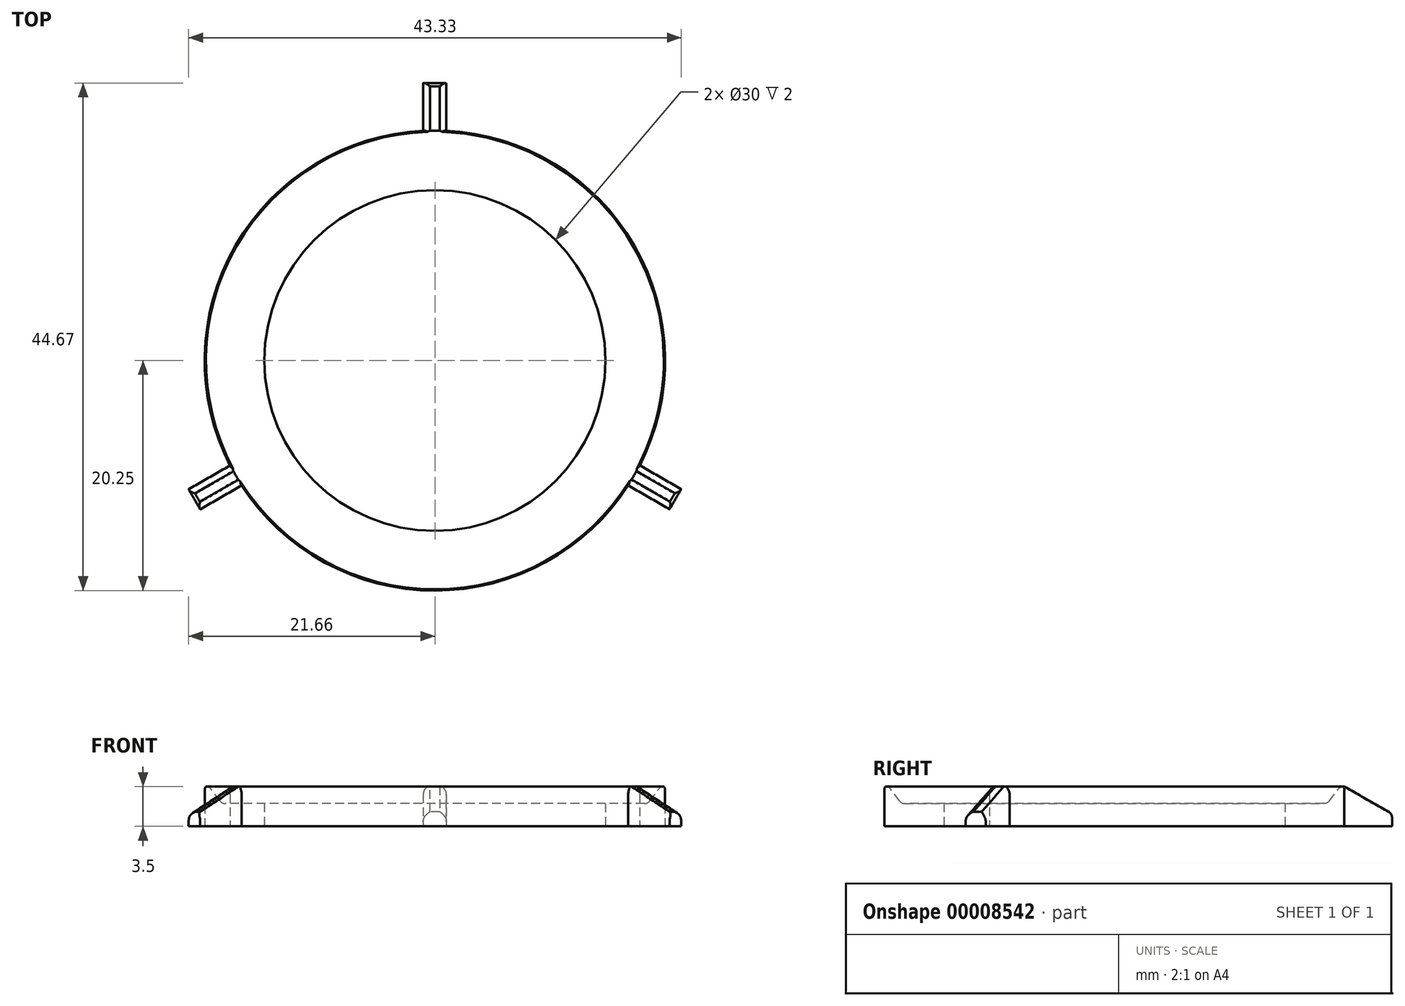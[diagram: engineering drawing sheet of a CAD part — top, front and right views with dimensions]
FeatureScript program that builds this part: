
annotation { "Feature Type Name" : "Feature", "Feature Type Description" : "" }
export const myFeature = defineFeature(function(context is Context, id is Id, definition is map)
    precondition{}
    {
        {
            var Q0;
            Q0=qCreatedBy(makeId("Top.planeOp"),FACE);
            var sketch = newSketch(context, id + "F0", { "sketchPlane" : qUnion([Q0])});
            skCircle(sketch, "E0", {"center": v(0, 0) * mm, "radius": 20.25 * mm});
            skCircle(sketch, "E1", {"center": v(0, 0) * mm, "radius": 15 * mm});
            skLineSegment(sketch, "E2", {"start": v(-1.03, 24.42) * mm, "end": v(-1.03, 20.22) * mm});
            skLineSegment(sketch, "E3", {"start": v(-1.03, 24.42) * mm, "end": v(0, 24.42) * mm});
            skLineSegment(sketch, "E4.trimOffspring", {"start": v(0, 24.4) * mm, "end": v(0, 24.42) * mm, "construction": true});
            skLineSegment(sketch, "E5", {"start": v(0, 24.42) * mm, "end": v(1.01, 24.42) * mm});
            skLineSegment(sketch, "E6", {"start": v(1.01, 24.42) * mm, "end": v(1.01, 20.22) * mm});
            skLineSegment(sketch, "E7.1.0", {"start": v(-20.64, -13.1) * mm, "end": v(-17, -11) * mm});
            skLineSegment(sketch, "E7.1.1", {"start": v(-20.64, -13.1) * mm, "end": v(-21.15, -12.22) * mm});
            skLineSegment(sketch, "E7.1.2", {"start": v(-21.15, -12.22) * mm, "end": v(-21.66, -11.34) * mm});
            skLineSegment(sketch, "E7.1.3", {"start": v(-21.66, -11.34) * mm, "end": v(-18.02, -9.24) * mm});
            skLineSegment(sketch, "E7.2.0", {"start": v(21.67, -11.32) * mm, "end": v(18.03, -9.22) * mm});
            skLineSegment(sketch, "E7.2.1", {"start": v(21.67, -11.32) * mm, "end": v(21.16, -12.2) * mm});
            skLineSegment(sketch, "E7.2.2", {"start": v(21.16, -12.2) * mm, "end": v(20.65, -13.09) * mm});
            skLineSegment(sketch, "E7.2.3", {"start": v(20.65, -13.09) * mm, "end": v(17, -10.99) * mm});
            skCircle(sketch, "E8", {"center": v(0, 0) * mm, "radius": 24.42 * mm, "construction": true});
            skLineSegment(sketch, "E9", {"start": v(0, 0) * mm, "end": v(0, 30.95) * mm, "construction": true});
            skSolve(sketch);
        }
        {
            var Q0;
            Q0 = qSketchRegion(id + "F0", true);
            extrude(context, id + "F1", {"entities" : qUnion([Q0]), "depth" : 6 * mm});
        }
        {
            var Q0;
            Q0=qCreatedBy(makeId("Right.planeOp"),FACE);
            var sketch = newSketch(context, id + "F2", { "sketchPlane" : qUnion([Q0])});
            skLineSegment(sketch, "E10.0.0", {"start": v(20.22, 0) * mm, "end": v(24.6, 0) * mm});
            skLineSegment(sketch, "E10.0.1", {"start": v(24.6, 0) * mm, "end": v(24.68, 6) * mm});
            skLineSegment(sketch, "E10.0.2", {"start": v(24.68, 6) * mm, "end": v(20.22, 6) * mm});
            skLineSegment(sketch, "E10.0.3", {"start": v(20.22, 6) * mm, "end": v(20.22, 0) * mm});
            skLineSegment(sketch, "E11", {"start": v(-15, 0) * mm, "end": v(-15, 6) * mm});
            skLineSegment(sketch, "E12", {"start": v(15, 6) * mm, "end": v(15, 0) * mm});
            skLineSegment(sketch, "E13.0.0", {"start": v(-9.22, 0) * mm, "end": v(20.22, 0) * mm});
            skLineSegment(sketch, "E13.0.1", {"start": v(20.22, 0) * mm, "end": v(20.22, 6) * mm});
            skLineSegment(sketch, "E13.0.2", {"start": v(20.22, 6) * mm, "end": v(-9.22, 6) * mm});
            skLineSegment(sketch, "E13.0.3", {"start": v(-9.22, 6) * mm, "end": v(-9.22, 0) * mm});
            skLineSegment(sketch, "E14", {"start": v(15, 2) * mm, "end": v(20.22, 2) * mm});
            skLineSegment(sketch, "E15", {"start": v(18.72, 2) * mm, "end": v(20.22, 4) * mm});
            skLineSegment(sketch, "E16", {"start": v(0, 0) * mm, "end": v(0, 9.56) * mm, "construction": true});
            skLineSegment(sketch, "E17", {"start": v(24.61, 1) * mm, "end": v(20.22, 3.5) * mm});
            skSolve(sketch);
        }
        {
            var Q0;
            {var subQ0=sQuery(id+"F2.wireOp",EDGE,"E10.0.2");Q0=makeQuery(id+"F2.imprint","IMPRINT",FACE,{"disambiguationData":[TD([[makeQuery(id+"F2.imprint","IMPRINT",EDGE,{"derivedFrom":subQ0}),1.0]])]});}
            var Q1;
            {var subQ5=sQuery(id+"F2.wireOp",EDGE,"E15");Q1=makeQuery(id+"F2.imprint","IMPRINT",FACE,{"disambiguationData":[TD([[makeQuery(id+"F2.imprint","IMPRINT",EDGE,{"derivedFrom":subQ5}),1.0]])]});}
            var Q2;
            Q2=sQuery(id+"F2.wireOp",EDGE,"E16");
            revolve(context, id + "F3", {"operationType" : NewBodyOperationType.REMOVE, "entities" : qUnion([Q0, Q1]), "axis" : qUnion([Q2]), "revolveType" : RevolveType.FULL, "oppositeDirection" : true});
        }
        {
            var Q0;
            Q0=makeQuery(id+"F3.boolean.opBoolean","COPY",EDGE,{"derivedFrom":makeQuery(id+"F3.opRevolve","SWEPT_EDGE",EDGE,{"disambiguationData":[OSD([sQuery(id+"F2.wireOp",EDGE,"E14"),sQuery(id+"F2.wireOp",EDGE,"E15")])]})});
            var Q1;
            Q1=makeQuery(id+"F3.boolean.opBoolean","COPY",EDGE,{"derivedFrom":makeQuery(id+"F3.opRevolve","SWEPT_EDGE",EDGE,{"disambiguationData":[OSD([sQuery(id+"F2.wireOp",EDGE,"E12"),sQuery(id+"F2.wireOp",EDGE,"E14")])]})});
            var Q2;
            Q2=makeQuery(id+"F3.boolean.opBoolean","COPY",EDGE,{"derivedFrom":makeQuery(id+"F3.opRevolve","SWEPT_EDGE",EDGE,{"disambiguationData":[OSD([sQuery(id+"F2.wireOp",EDGE,"E13.0.1"),sQuery(id+"F2.wireOp",EDGE,"E15")])]})});
            var Q3;
            Q3=makeQuery(id+"F3.boolean.opBoolean","INTERSECT",EDGE,{"derivedFrom":[makeQuery(id+"F1.opExtrude","SWEPT_FACE",FACE,{"disambiguationData":[OSD([sQuery(id+"F0.wireOp",EDGE,"E2")])]}),makeQuery(id+"F3.opRevolve","SWEPT_FACE",FACE,{"disambiguationData":[OSD([sQuery(id+"F2.wireOp",EDGE,"E17")])]})]});
            var Q4;
            Q4=makeQuery(id+"F3.boolean.opBoolean","INTERSECT",EDGE,{"derivedFrom":[makeQuery(id+"F1.opExtrude","SWEPT_FACE",FACE,{"disambiguationData":[OSD([sQuery(id+"F0.wireOp",EDGE,"E6")])]}),makeQuery(id+"F3.opRevolve","SWEPT_FACE",FACE,{"disambiguationData":[OSD([sQuery(id+"F2.wireOp",EDGE,"E17")])]})]});
            var Q5;
            Q5=makeQuery(id+"F3.boolean.opBoolean","INTERSECT",EDGE,{"derivedFrom":[makeQuery(id+"F1.opExtrude","SWEPT_FACE",FACE,{"disambiguationData":[OSD([sQuery(id+"F0.wireOp",EDGE,"E3"),sQuery(id+"F0.wireOp",EDGE,"E5")])]}),makeQuery(id+"F3.opRevolve","SWEPT_FACE",FACE,{"disambiguationData":[OSD([sQuery(id+"F2.wireOp",EDGE,"E17")])]})]});
            var Q6;
            Q6=makeQuery(id+"F3.boolean.opBoolean","INTERSECT",EDGE,{"derivedFrom":[makeQuery(id+"F1.opExtrude","SWEPT_FACE",FACE,{"disambiguationData":[OSD([sQuery(id+"F0.wireOp",EDGE,"E7.2.0")])]}),makeQuery(id+"F3.opRevolve","SWEPT_FACE",FACE,{"disambiguationData":[OSD([sQuery(id+"F2.wireOp",EDGE,"E17")])]})]});
            var Q7;
            Q7=makeQuery(id+"F3.boolean.opBoolean","INTERSECT",EDGE,{"derivedFrom":[makeQuery(id+"F1.opExtrude","SWEPT_FACE",FACE,{"disambiguationData":[OSD([sQuery(id+"F0.wireOp",EDGE,"E7.2.1"),sQuery(id+"F0.wireOp",EDGE,"E7.2.2")])]}),makeQuery(id+"F3.opRevolve","SWEPT_FACE",FACE,{"disambiguationData":[OSD([sQuery(id+"F2.wireOp",EDGE,"E17")])]})]});
            var Q8;
            Q8=makeQuery(id+"F3.boolean.opBoolean","INTERSECT",EDGE,{"derivedFrom":[makeQuery(id+"F1.opExtrude","SWEPT_FACE",FACE,{"disambiguationData":[OSD([sQuery(id+"F0.wireOp",EDGE,"E7.2.3")])]}),makeQuery(id+"F3.opRevolve","SWEPT_FACE",FACE,{"disambiguationData":[OSD([sQuery(id+"F2.wireOp",EDGE,"E17")])]})]});
            var Q9;
            Q9=makeQuery(id+"F3.boolean.opBoolean","INTERSECT",EDGE,{"derivedFrom":[makeQuery(id+"F1.opExtrude","SWEPT_FACE",FACE,{"disambiguationData":[OSD([sQuery(id+"F0.wireOp",EDGE,"E7.1.1"),sQuery(id+"F0.wireOp",EDGE,"E7.1.2")])]}),makeQuery(id+"F3.opRevolve","SWEPT_FACE",FACE,{"disambiguationData":[OSD([sQuery(id+"F2.wireOp",EDGE,"E17")])]})]});
            var Q10;
            Q10=makeQuery(id+"F3.boolean.opBoolean","INTERSECT",EDGE,{"derivedFrom":[makeQuery(id+"F1.opExtrude","SWEPT_FACE",FACE,{"disambiguationData":[OSD([sQuery(id+"F0.wireOp",EDGE,"E7.1.3")])]}),makeQuery(id+"F3.opRevolve","SWEPT_FACE",FACE,{"disambiguationData":[OSD([sQuery(id+"F2.wireOp",EDGE,"E17")])]})]});
            var Q11;
            Q11=makeQuery(id+"F3.boolean.opBoolean","INTERSECT",EDGE,{"derivedFrom":[makeQuery(id+"F1.opExtrude","SWEPT_FACE",FACE,{"disambiguationData":[OSD([sQuery(id+"F0.wireOp",EDGE,"E7.1.0")])]}),makeQuery(id+"F3.opRevolve","SWEPT_FACE",FACE,{"disambiguationData":[OSD([sQuery(id+"F2.wireOp",EDGE,"E17")])]})]});
            fillet(context, id + "F4", {"entities" : qUnion([Q0, Q1, Q2, Q3, Q4, Q5, Q6, Q7, Q8, Q9, Q10, Q11]), "radius" : .6 * mm, "tangentPropagation" : true, "allowEdgeOverflow" : false});
        }
        {
            var Q0;
            {var subQ0=sQuery(id+"F0.wireOp",EDGE,"E0");Q0=makeQuery(id+"F3.boolean.opBoolean","INTERSECT",EDGE,{"derivedFrom":[makeQuery(id+"F1.opExtrude","SWEPT_FACE",FACE,{"disambiguationData":[OSD([subQ0]),TDD([makeQuery(id+"F0.imprint","IMPRINT",EDGE,{"disambiguationData":[TD([[makeQuery(id+"F0.imprint","INTERSECT",VERTEX,{"derivedFrom":[subQ0,sQuery(id+"F0.wireOp",EDGE,"E2")]}),-1.0]])],"derivedFrom":subQ0})])]}),makeQuery(id+"F3.opRevolve","SWEPT_FACE",FACE,{"disambiguationData":[OSD([sQuery(id+"F2.wireOp",EDGE,"E17")])]})]});}
            var Q1;
            {var subQ0=sQuery(id+"F0.wireOp",EDGE,"E0");Q1=makeQuery(id+"F3.boolean.opBoolean","INTERSECT",EDGE,{"derivedFrom":[makeQuery(id+"F1.opExtrude","SWEPT_FACE",FACE,{"disambiguationData":[OSD([subQ0]),TDD([makeQuery(id+"F0.imprint","IMPRINT",EDGE,{"disambiguationData":[TD([[makeQuery(id+"F0.imprint","INTERSECT",VERTEX,{"derivedFrom":[subQ0,sQuery(id+"F0.wireOp",EDGE,"E7.1.0")]}),-1.0]])],"derivedFrom":subQ0})])]}),makeQuery(id+"F3.opRevolve","SWEPT_FACE",FACE,{"disambiguationData":[OSD([sQuery(id+"F2.wireOp",EDGE,"E17")])]})]});}
            var Q2;
            {var subQ0=sQuery(id+"F0.wireOp",EDGE,"E0");Q2=makeQuery(id+"F3.boolean.opBoolean","INTERSECT",EDGE,{"derivedFrom":[makeQuery(id+"F1.opExtrude","SWEPT_FACE",FACE,{"disambiguationData":[OSD([subQ0]),TDD([makeQuery(id+"F0.imprint","IMPRINT",EDGE,{"disambiguationData":[TD([[makeQuery(id+"F0.imprint","INTERSECT",VERTEX,{"derivedFrom":[subQ0,sQuery(id+"F0.wireOp",EDGE,"E6")]}),1.0]])],"derivedFrom":subQ0})])]}),makeQuery(id+"F3.opRevolve","SWEPT_FACE",FACE,{"disambiguationData":[OSD([sQuery(id+"F2.wireOp",EDGE,"E17")])]})]});}
            fillet(context, id + "F5", {"entities" : qUnion([Q0, Q1, Q2]), "radius" : .5 * mm, "tangentPropagation" : true, "allowEdgeOverflow" : false});
        }
    });
